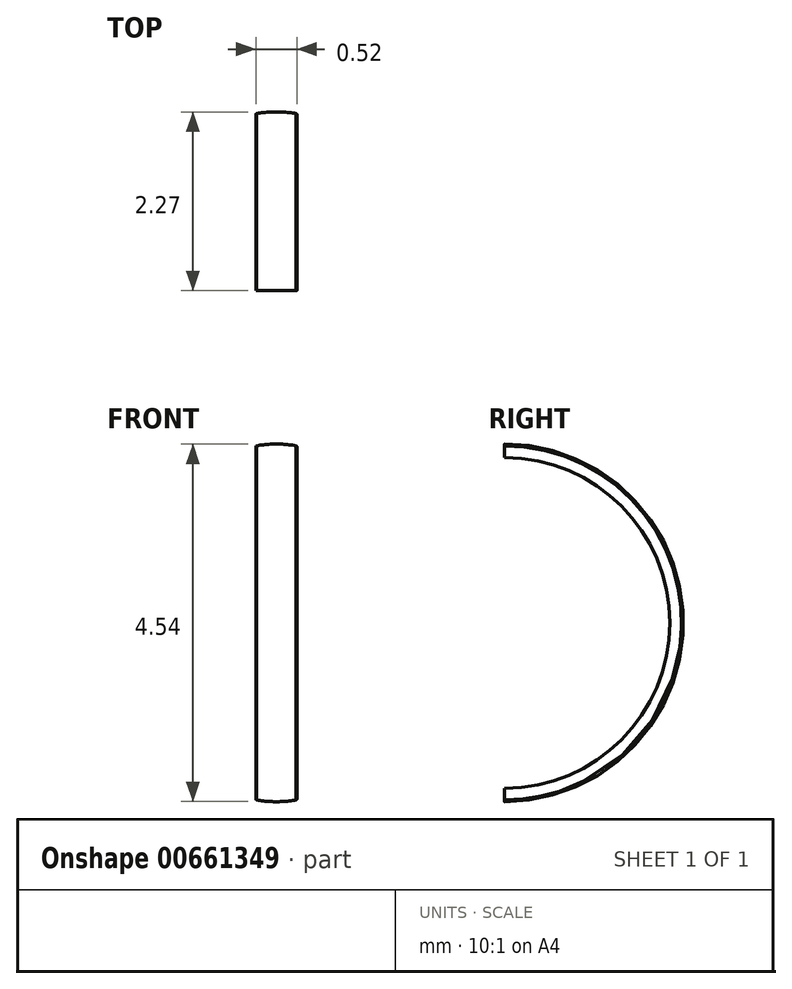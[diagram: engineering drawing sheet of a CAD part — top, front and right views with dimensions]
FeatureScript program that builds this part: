
annotation { "Feature Type Name" : "Feature", "Feature Type Description" : "" }
export const myFeature = defineFeature(function(context is Context, id is Id, definition is map)
    precondition{}
    {
        {
            var Q0;
            Q0=qCreatedBy(makeId("Front.planeOp"),FACE);
            var sketch = newSketch(context, id + "F0", { "sketchPlane" : qUnion([Q0])});
            skLineSegment(sketch, "E0", {"start": v(0, 0) * mm, "end": v(0, -2.25) * mm, "construction": true});
            skLineSegment(sketch, "E1", {"start": v(-0.26, -2.24) * mm, "end": v(-0.26, -2.1) * mm});
            skLineSegment(sketch, "E2", {"start": v(-0.62, 0) * mm, "end": v(1.8, 0) * mm, "construction": true});
            skPoint(sketch, "E3.visualSharp", {"position": v(-0.26, -2.25) * mm});
            skArc(sketch, "E3.filletArc", {"start": v(-0.26, -2.24) * mm, "mid": v(-0.26, -2.25) * mm, "end": v(-0.25, -2.25) * mm});
            skLineSegment(sketch, "E4.MirrorCS", {"start": v(-0.26, 2.24) * mm, "end": v(-0.26, 2.1) * mm});
            skArc(sketch, "E5.MirrorCS", {"start": v(-0.26, 2.24) * mm, "mid": v(-0.26, 2.25) * mm, "end": v(-0.25, 2.25) * mm});
            skFitSpline(sketch, "E6.MirrorCS", {"points": [v(-0.25, 2.25) * mm, v(0, 2.26) * mm], "startDerivative": vector(0.08, 0.01) * mm, "endDerivative": vector(0.25, 0) * mm});
            skLineSegment(sketch, "E7.MirrorCS", {"start": v(0.26, -2.24) * mm, "end": v(0.26, -2.1) * mm});
            skArc(sketch, "E8.MirrorCS", {"start": v(0.26, -2.24) * mm, "mid": v(0.26, -2.25) * mm, "end": v(0.25, -2.25) * mm});
            skFitSpline(sketch, "E9", {"points": [v(-0.25, -2.25) * mm, v(0.25, -2.25) * mm], "startDerivative": vector(0.53, -0.09) * mm, "endDerivative": vector(0.53, 0.09) * mm});
            skSolve(sketch);
        }
        {
            var Q0;
            Q0=sQuery(id+"F0.wireOp",EDGE,"E1");
            var Q1;
            Q1=sQuery(id+"F0.wireOp",EDGE,"E3.filletArc");
            var Q2;
            Q2=sQuery(id+"F0.wireOp",EDGE,"E9");
            var Q3;
            Q3=sQuery(id+"F0.wireOp",EDGE,"E8.MirrorCS");
            var Q4;
            Q4=sQuery(id+"F0.wireOp",EDGE,"E7.MirrorCS");
            var Q5;
            Q5=sQuery(id+"F0.wireOp",EDGE,"E2");
            revolve(context, id + "F1", {"bodyType" : ToolBodyType.SURFACE, "surfaceEntities" : qUnion([Q0, Q1, Q2, Q3, Q4]), "axis" : qUnion([Q5]), "revolveType" : RevolveType.ONE_DIRECTION, "angle" : 180 * degree});
        }
    });
